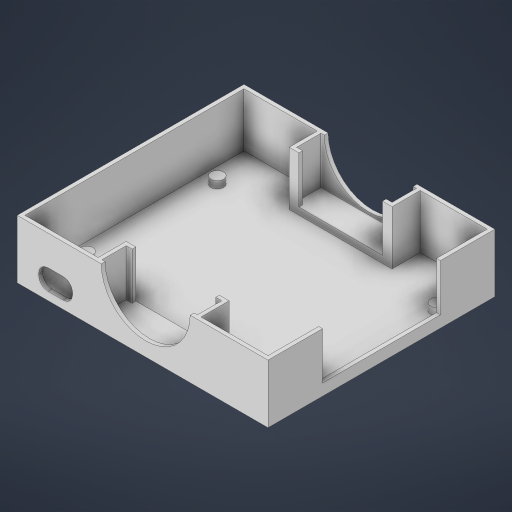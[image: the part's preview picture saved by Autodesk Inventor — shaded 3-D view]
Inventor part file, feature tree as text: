
AUTODESK INVENTOR PART (.ipt)
format: ipt  version: 2023 (Build 270158000, 158)  size: 388,096 bytes
history: native  units: in
note: dims shown in document units (in); Inventor stores cm internally (conversion verified against a paired STEP export)
features: extrude x12, sketch x12, reference x11, other x5, plane x3, projected_geometry x2
ambient origin geometry x8: Origin, YZ Plane, XZ Plane, XY Plane, X Axis, Y Axis, Z Axis, Center Point
bodies: Solid1 (feature_tree)
feature tree (45):
  plane  "Work Plane1"
  extrude  "Extrusion1"  Depth=0.04in
  extrude  "Extrusion2"  Depth=0.5512in
  extrude  "Extrusion3"  Depth=0.065in
  extrude  "Extrusion4"  TaperAngle=0.0deg  [1 undecoded]
  extrude  "Extrusion5"  Depth=0.7874in TaperAngle=0.0deg
  extrude  "Extrusion6"  Depth=0.1969in TaperAngle=0.0deg
  sketch  "Sketch7"  dims[d16=0.05in d17=0.1181in d18=0.0in]
  plane  "Work Plane2"
  extrude  "Extrusion7"  Depth=0.1181in TaperAngle=0.0deg
  extrude  "Extrusion8"  Depth=0.1181in TaperAngle=0.0deg
  extrude  "Extrusion9"  Depth=0.1181in TaperAngle=0.0deg
  sketch  "Sketch10"  dims[d28=1.7853in d29=0.05in]
  plane  "Work Plane3"
  extrude  "Extrusion10"  Depth=0.05in
  extrude  "Extrusion11"  Depth=0.05in
  extrude  "Extrusion12"  Depth=0.1in
  sketch  "Sketch1"  dims[d0=0.04in d1=0.04in]
  reference  "Reference1"
  reference  "Reference2"
  sketch  "Sketch2"  dims[d2=0.5512in d3=0.5512in]
  projected_geometry  "Projected Loop1"
  sketch  "Sketch3"  dims[d5=0.065in d6=0.065in]
  sketch  "Sketch4"  dims[d7=0.065in d8=0.0in]
  reference  "Reference3"
  reference  "Reference4"
  reference  "Reference5"
  reference  "Reference6"
  sketch  "Sketch5"  dims[d9=0.065in d10=0.7874in d11=0.0in]
  reference  "Reference7"
  reference  "Reference8"
  reference  "Reference9"
  sketch  "Sketch6"  dims[d12=0.1969in d13=0.0in d14=0.0787in d15=0.0in]
  reference  "Reference10"
  reference  "Reference11"
  sketch  "Sketch8"  dims[d19=0.6378in d22=0.1181in d23=0.0in]
  projected_geometry  "Projected Loop2"
  sketch  "Sketch9"  dims[d24=0.05in d25=0.1181in d26=0.0in]
  sketch  "Sketch11"  dims[d30=0.15in d31=0.05in]
  sketch  "Sketch12"  dims[d32=1.7323in d33=0.8661in d34=0.4724in d35=1.0in d36=0.0in d45=1.0in d46=0.0in d47=0.1in d48=0.1in d49=0.063in d50=0.063in d51=0.063in d52=0.063in d53=1.4961in d54=1.0in d55=0.0in d56=0.4724in d57=1.7323in d58=0.8661in d59=1.0in d60=0.0in d62=0.063in d63=0.1in d64=0.063in d65=0.063in d66=0.063in d67=0.1in d68=1.0in d69=0.0in d70=1.4961in d71=1.0in d72=0.0in]
  other  "<userpath>\Documents\Inventor\2024 Mavericks\Orange PI\OrangePICover.iam"
  other  "OrangePICover.iam"
  other  "OPi5_pcb_asm-0809:1"
  other  "orangepicover-002:1"
  other  "Assembly10"
note: 1 required parameter value undecoded (feature->parameter linkage not recoverable at this tier; creation-order binding heuristic only, values carry confidence <= 0.55)
